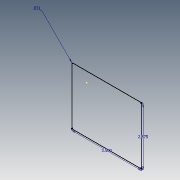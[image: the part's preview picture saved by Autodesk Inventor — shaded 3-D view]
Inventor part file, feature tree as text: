
AUTODESK INVENTOR PART (.ipt)
format: ipt  version: 2013 SP2 (Build 170200200, 200)  size: 99,840 bytes
history: native  units: in
note: dims shown in document units (in); Inventor stores cm internally (conversion verified against a paired STEP export)
features: sketch x1
ambient origin geometry x8: Origin, YZ Plane, XZ Plane, XY Plane, X Axis, Y Axis, Z Axis, Center Point
feature tree (1):
  sketch  "Sketch1"  dims[d0=3.5in d1=2.875in d2=0.0312in]
